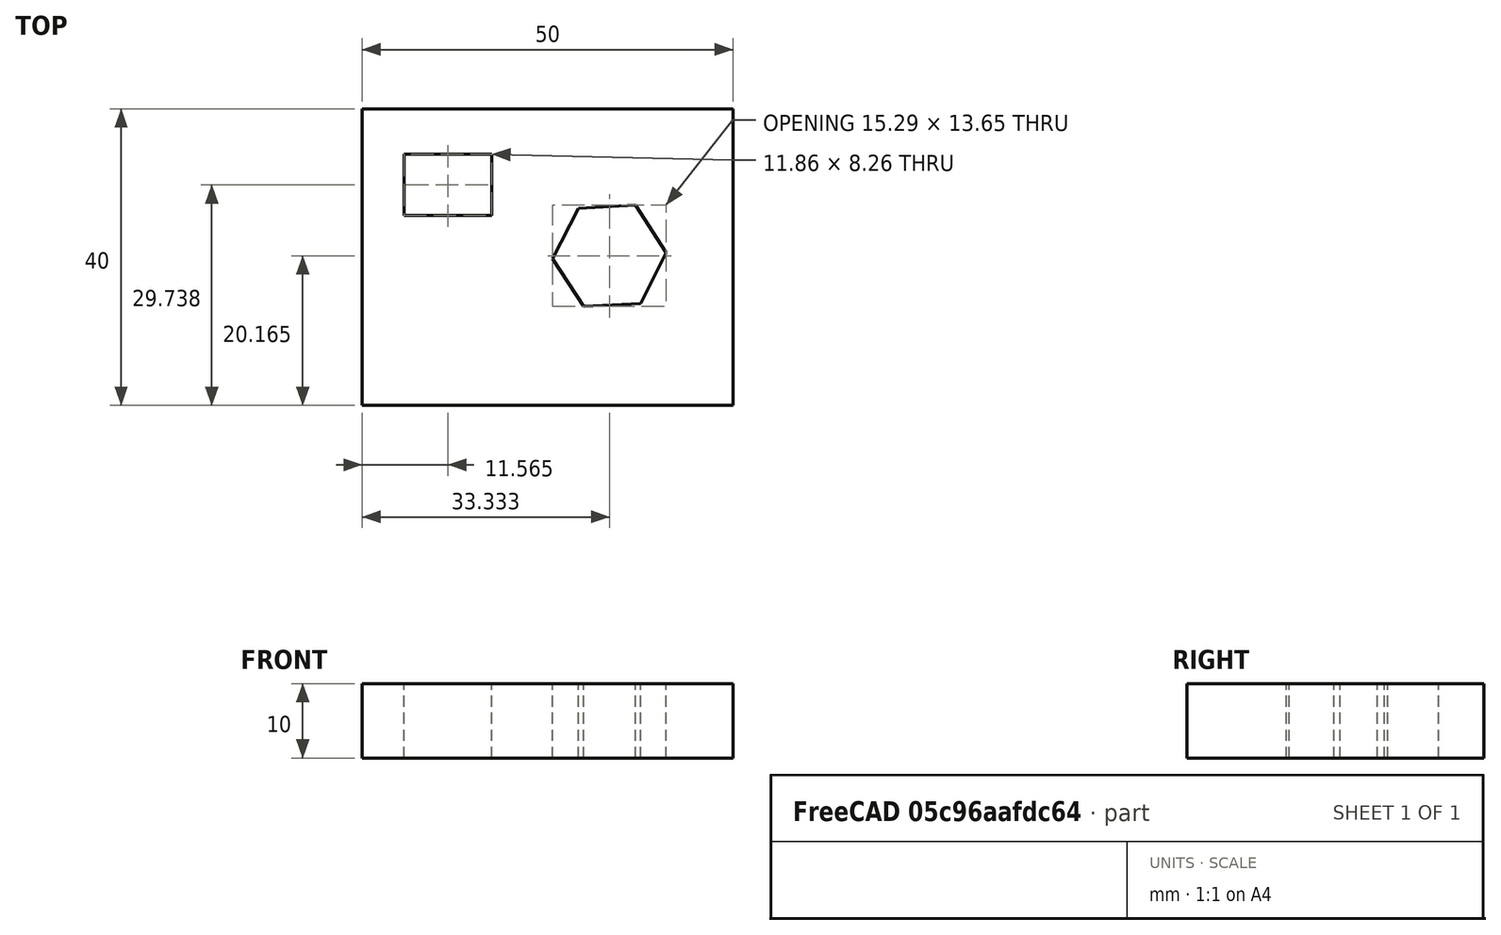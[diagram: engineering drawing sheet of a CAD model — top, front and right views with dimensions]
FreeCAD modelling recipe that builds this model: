
FCSTD DOCUMENT  (FreeCAD 0.20RUnknown)
Label: Holes
License: All rights reserved
LicenseURL: http://en.wikipedia.org/wiki/All_rights_reserved
objects: Sketcher::SketchObject×1, PartDesign::Pad×1, PartDesign::Body×1
note: 4 computed .brp shape members not serialized (recipe doc carries the construction recipe); baked Part::Feature solids carry a one-line shape summary decoded from their .brp

FEATURE [Sketcher::SketchObject] Sketch
  FullyConstrained = false
  MapMode = 5
  Support = -> [XY_Plane]
  sketch-geometry (15):
    g0: LineSegment StartX=0 StartY=40 StartZ=0 EndX=50 EndY=40 EndZ=0
    g1: LineSegment StartX=50 StartY=40 StartZ=0 EndX=50 EndY=0 EndZ=0
    g2: LineSegment StartX=50 StartY=0 StartZ=0 EndX=0 EndY=0 EndZ=0
    g3: LineSegment StartX=0 StartY=0 StartZ=0 EndX=0 EndY=40 EndZ=0
    g4: LineSegment StartX=5.63654 StartY=33.8678 StartZ=0 EndX=17.4927 EndY=33.8678 EndZ=0
    g5: LineSegment StartX=17.4927 StartY=33.8678 StartZ=0 EndX=17.4927 EndY=25.6074 EndZ=0
    g6: LineSegment StartX=17.4927 StartY=25.6074 StartZ=0 EndX=5.63654 EndY=25.6074 EndZ=0
    g7: LineSegment StartX=5.63654 StartY=25.6074 StartZ=0 EndX=5.63654 EndY=33.8678 EndZ=0
    g8: LineSegment StartX=37.5121 StartY=13.7512 StartZ=0 EndX=40.9774 EndY=20.5772 EndZ=0
    g9: LineSegment StartX=40.9774 StartY=20.5772 StartZ=0 EndX=36.7986 EndY=26.9912 EndZ=0
    g10: LineSegment StartX=36.7986 StartY=26.9912 StartZ=0 EndX=29.1545 EndY=26.5792 EndZ=0
    g11: LineSegment StartX=29.1545 StartY=26.5792 StartZ=0 EndX=25.6892 EndY=19.7533 EndZ=0
    g12: LineSegment StartX=25.6892 StartY=19.7533 StartZ=0 EndX=29.8681 EndY=13.3393 EndZ=0
    g13: LineSegment StartX=29.8681 StartY=13.3393 StartZ=0 EndX=37.5121 EndY=13.7512 EndZ=0
    g14: Circle CenterX=33.3333 CenterY=20.1652 CenterZ=0 NormalX=0 NormalY=0 NormalZ=1 AngleXU=0 Radius=7.65518
  constraints (32):
    c: Coincident(g0,g1)
    c: Coincident(g1,g2)
    c: Coincident(g2,g3)
    c: Coincident(g3,g0)
    c: Horizontal(g0)
    c: Horizontal(g2)
    c: Vertical(g1)
    c: Vertical(g3)
    c: Coincident(g2,g-1)
    c: DistanceY(g3,g3) = 40
    c: DistanceX(g2,g2) = 50
    c: Coincident(g4,g5)
    c: Coincident(g5,g6)
    c: Coincident(g6,g7)
    c: Coincident(g7,g4)
    c: Horizontal(g4)
    c: Horizontal(g6)
    c: Vertical(g5)
    c: Vertical(g7)
    c: Coincident(g8,g9)
    c: Coincident(g9,g10)
    c: Coincident(g10,g11)
    c: Coincident(g11,g12)
    c: Coincident(g12,g13)
    c: Coincident(g13,g8)
    c: Equal(g8, g9-g13) x5
    c: PointOnObject(g8,g14)
    c: PointOnObject(g9,g14)
    c: PointOnObject(g10,g14)
    c: PointOnObject(g11,g14)
    c: PointOnObject(g12,g14)
    c: PointOnObject(g13,g14)
FEATURE [PartDesign::Pad] Pad
  Direction = (0,0,1)
  Length = 10
  Length2 = 10
  Profile = -> Sketch
  ReferenceAxis = -> Sketch [N_Axis]
  Type = 0
FEATURE [PartDesign::Body] Body
  Group = -> [Sketch,Pad]
  Origin = -> Origin
  Tip = -> Pad
